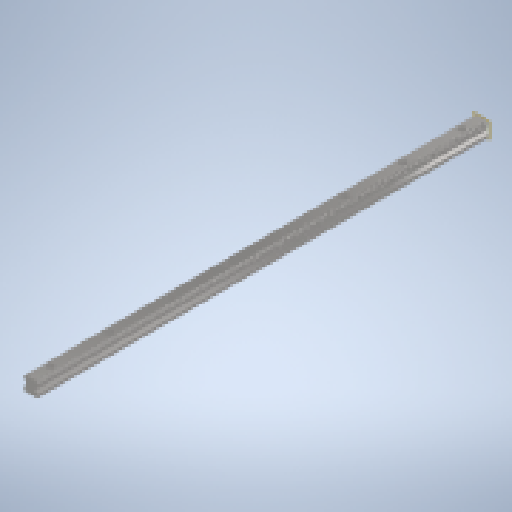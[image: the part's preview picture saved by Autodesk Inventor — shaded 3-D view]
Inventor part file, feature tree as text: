
AUTODESK INVENTOR PART (.ipt)
format: ipt  version: 2024 (Build 280153000, 153)  size: 217,088 bytes
history: native  units: mm
features: plane x1, split x1, other x1
ambient origin geometry x8: Origin, YZ Plane, XZ Plane, XY Plane, X Axis, Y Axis, Z Axis, Center Point
bodies: Solid1 (feature_tree)
feature tree (3):
  plane  "Work Plane1"
  split  "Split1"
  other  "LPattern1"
